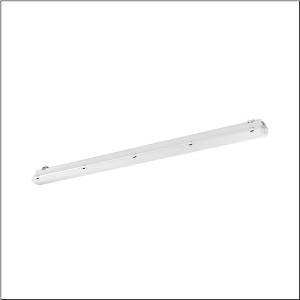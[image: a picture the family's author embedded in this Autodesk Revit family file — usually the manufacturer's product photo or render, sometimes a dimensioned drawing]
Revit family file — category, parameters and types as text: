
# Revit family: monsun_r__11xtreme_mo_51fe10dp460j_08a3
name_source: partatom
category: Lighting Fixtures
units: mm (PartAtom-declared; Revit-internal decimal feet)

## family parameters
Cut with Voids When Loaded = No
Host = Face
Light Source = No
Part Type = Normal
Room Calculation Point = No
Round Connector Dimension = Use Diameter
Shared = No

## types (1)
- --- (1 x LED, 6370 lm, 36.5 W, 4000K)
    Apparent Load = 37 VA
    CIE Flux Codes = 47 77 93 94 100
    Color Rendering = 80
    Color Temperature = 4000K
    Default Elevation = 1800 mm
    Description = Monsun® 11Xtreme MO, damp-proof luminaire, chain hanger, primary optical cover: enclosure, of PMMA, light emission: direct distribution, primary light characteristic: symmetric, installation type: suspended mounting, surface-mounted, horizontal mounting, vertical mounting, LED, rated luminous flux: 6.370lm, luminous efficacy: 175lm/W, light colour: 840, colour temperature: 4000K, control gear: ECG DALI, with terminal, 5-pole, max. 2.5mm², mains connection: 220..240V, AC, 50/60Hz, rated input power: 37W, luminaire housing, of glass-fibre reinforced polyester, uncoated, bright grey, incl. chain hanger, length: 1.590mm, width: 90mm, height: 88mm, clip for enclosure, of stainless steel (V2A), ceiling mounting element, of stainless steel (V2A), chain hanger, of stainless steel (V2A), protection rating (complete): IP66, insulation class (complete): insulation class I (protective earthing), certification: CE, ENEC, VDE, UKCA, protection symbol: D, impact resistance: IK04, permissible operating ambient temperature: -35..+55°C, standard: EN 60598-2-1, EN 50419, corresponds to IFS (International Featured Standards) requirements for safety and quality in the food industry, for indoor or canopied outdoor use, no direct snow, no direct sun, no direct rain, contact your sales advisor before using the luminaires in applications with unclear chemical exposure, large temperature fluctuations or condensation-forming humidity, LABS conformity tested according to VDMA 24364:2018-05, packaging unit: 1 piece
    Height = 88 mm
    Lamp = 1 x LED
    Lamp Light Flux = 6370 lm
    Lamp Power = 36.5 W
    Lamp count = 1
    Length = 1590 mm
    Luminous efficacy = 175 lm/W
    Manufacturer = Siteco
    ModVariant = No
    Model = 51FE10DP460J
    Mounting Place = Ceiling
    Mounting Type = Surface mounted
    Number of Poles = 1
    OnlyDefault = Yes
    Power Factor = 1
    Product Name = Monsun® 11Xtreme MO
    Product group = damp-proof luminaire
    ProductGroupID = 300
    Protection Class = Protection class I
    Protection Degree = IP 66
    RLX_Detail_Level = 1
    RLX_Emergency_Light_Flux = 0 lm
    RLX_Emergency_Type = 0
    RLX_Emergency_Type_DB = No
    RlxData = <blob elided: 87185 chars, md5=dbb8375c>
    Socket = socket
    Standby Power = 0 W
    System Light Flux = 6370 lm
    System Power = 37 W
    Type Comments = factory setting: luminous flux: 100 % | dim-lin: 254 | 240 mA
    Type Image = l_1319630.jpg
    URL = http://relux.com
    VarID = @adj_170343
    Voltage = 0 V
    Weight = 0.00 kg
    Width = 90 mm

## geometry (parser evidence)
native form markers: Blend x4, Sweep x15
no freeform markers — native parametric forms only
